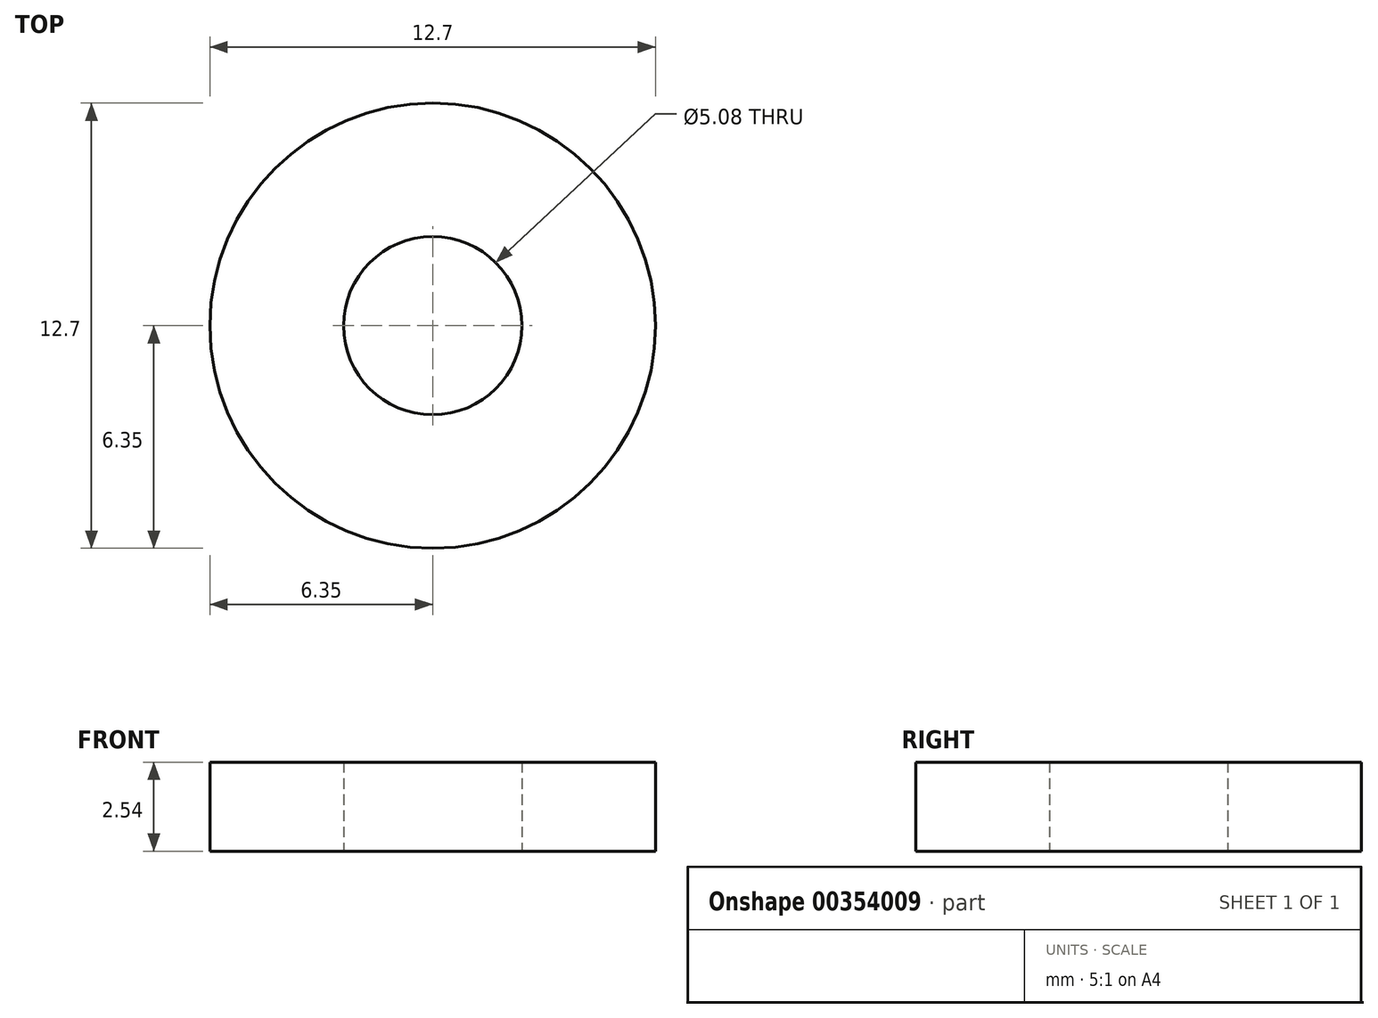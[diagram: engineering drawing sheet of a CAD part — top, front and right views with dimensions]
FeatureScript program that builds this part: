
annotation { "Feature Type Name" : "Feature", "Feature Type Description" : "" }
export const myFeature = defineFeature(function(context is Context, id is Id, definition is map)
    precondition{}
    {
        {
            var Q0;
            Q0=qCreatedBy(makeId("Top.planeOp"),FACE);
            var sketch = newSketch(context, id + "F0", { "sketchPlane" : qUnion([Q0])});
            skCircle(sketch, "E0", {"center": v(0, 0) * mm, "radius": 6.35 * mm});
            skCircle(sketch, "E1", {"center": v(0, 0) * mm, "radius": 2.54 * mm});
            skSolve(sketch);
        }
        {
            var Q0;
            Q0=makeQuery(id+"F0.imprint","IMPRINT",FACE,{"disambiguationData":[TD([[makeQuery(id+"F0.imprint","IMPRINT",EDGE,{"derivedFrom":sQuery(id+"F0.wireOp",EDGE,"E0")}),1.0]])]});
            extrude(context, id + "F1", {"entities" : qUnion([Q0]), "depth" : 2.54 * mm});
        }
    });
